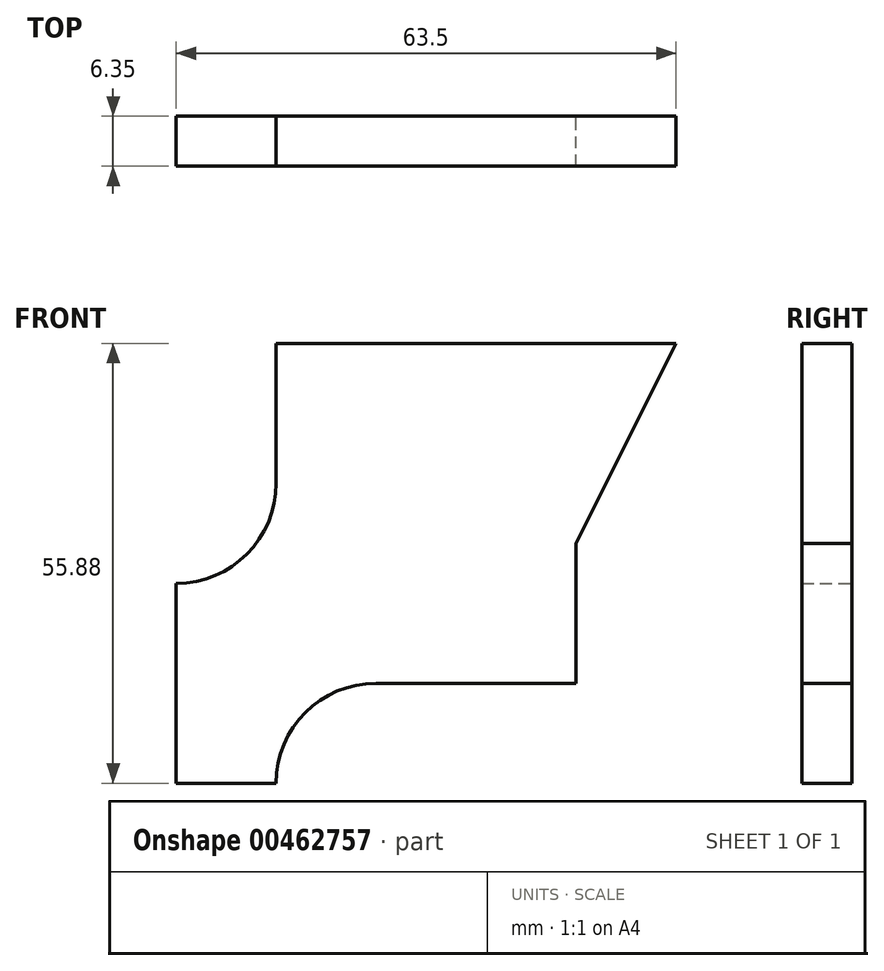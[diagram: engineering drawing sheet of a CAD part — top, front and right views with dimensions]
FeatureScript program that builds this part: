
annotation { "Feature Type Name" : "Feature", "Feature Type Description" : "" }
export const myFeature = defineFeature(function(context is Context, id is Id, definition is map)
    precondition{}
    {
        {
            var Q0;
            Q0=qCreatedBy(makeId("Front.planeOp"),FACE);
            var sketch = newSketch(context, id + "F0", { "sketchPlane" : qUnion([Q0])});
            skLineSegment(sketch, "E0", {"start": v(0, 0) * mm, "end": v(12.7, 0) * mm});
            skLineSegment(sketch, "E1", {"start": v(12.7, 55.88) * mm, "end": v(63.5, 55.88) * mm});
            skLineSegment(sketch, "E2", {"start": v(0, 0) * mm, "end": v(0, 25.4) * mm});
            skLineSegment(sketch, "E3", {"start": v(0, 25.4) * mm, "end": v(0, 25.4) * mm});
            skLineSegment(sketch, "E4", {"start": v(12.7, 55.88) * mm, "end": v(12.7, 38.1) * mm});
            skLineSegment(sketch, "E5", {"start": v(12.7, 0) * mm, "end": v(12.7, 0) * mm});
            skLineSegment(sketch, "E6", {"start": v(25.4, 12.7) * mm, "end": v(25.4, 12.7) * mm});
            skArc(sketch, "E7.filletArc", {"start": v(25.4, 12.7) * mm, "mid": v(16.42, 8.98) * mm, "end": v(12.7, 0) * mm});
            skArc(sketch, "E8.filletArc", {"start": v(0, 25.4) * mm, "mid": v(8.98, 29.12) * mm, "end": v(12.7, 38.1) * mm});
            skLineSegment(sketch, "E9", {"start": v(25.4, 12.7) * mm, "end": v(50.8, 12.7) * mm});
            skLineSegment(sketch, "E10", {"start": v(50.8, 12.7) * mm, "end": v(50.8, 30.48) * mm});
            skLineSegment(sketch, "E11", {"start": v(63.5, 55.88) * mm, "end": v(50.8, 30.48) * mm});
            skSolve(sketch);
        }
        {
            var Q0;
            Q0 = qSketchRegion(id + "F0", true);
            extrude(context, id + "F1", {"entities" : qUnion([Q0]), "depth" : 6.35 * mm});
        }
    });
